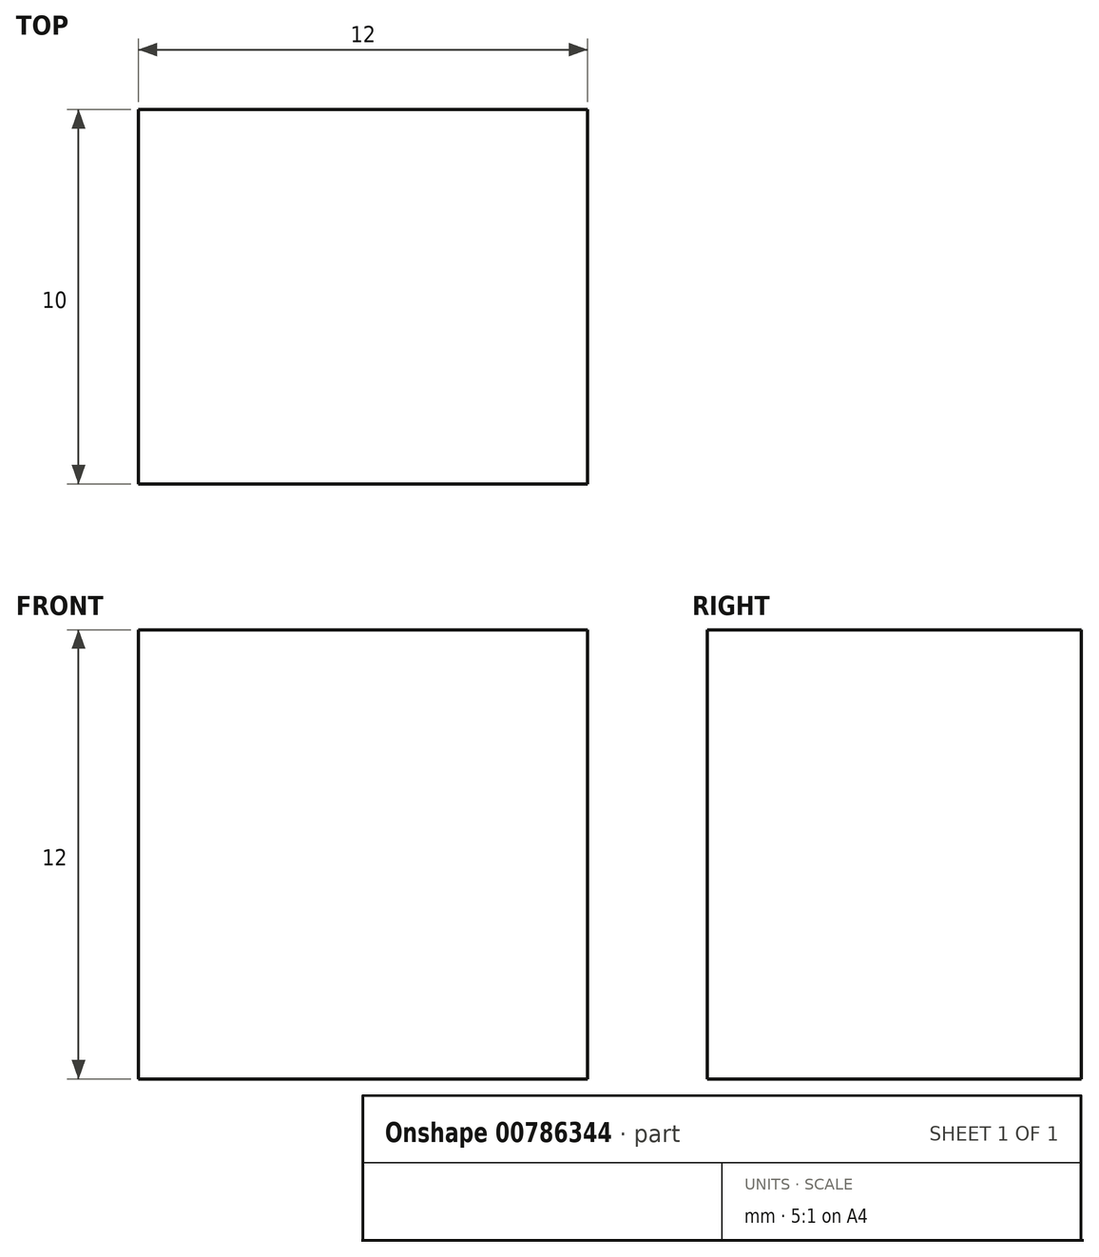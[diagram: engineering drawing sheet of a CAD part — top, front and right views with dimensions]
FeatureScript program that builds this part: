
annotation { "Feature Type Name" : "Feature", "Feature Type Description" : "" }
export const myFeature = defineFeature(function(context is Context, id is Id, definition is map)
    precondition{}
    {
        {
            var Q0;
            Q0=qCreatedBy(makeId("Front.planeOp"),FACE);
            var sketch = newSketch(context, id + "F0", { "sketchPlane" : qUnion([Q0])});
            skLineSegment(sketch, "E0.bottom", {"start": v(0, 0) * mm, "end": v(12, 0) * mm});
            skLineSegment(sketch, "E0.top", {"start": v(0, 12) * mm, "end": v(12, 12) * mm});
            skLineSegment(sketch, "E0.left", {"start": v(0, 0) * mm, "end": v(0, 12) * mm});
            skLineSegment(sketch, "E0.right", {"start": v(12, 0) * mm, "end": v(12, 12) * mm});
            skSolve(sketch);
        }
        {
            var Q0;
            Q0 = qSketchRegion(id + "F0", true);
            extrude(context, id + "F1", {"entities" : qUnion([Q0]), "depth" : 10 * mm, "offsetDistance" : 25 * mm});
        }
    });
